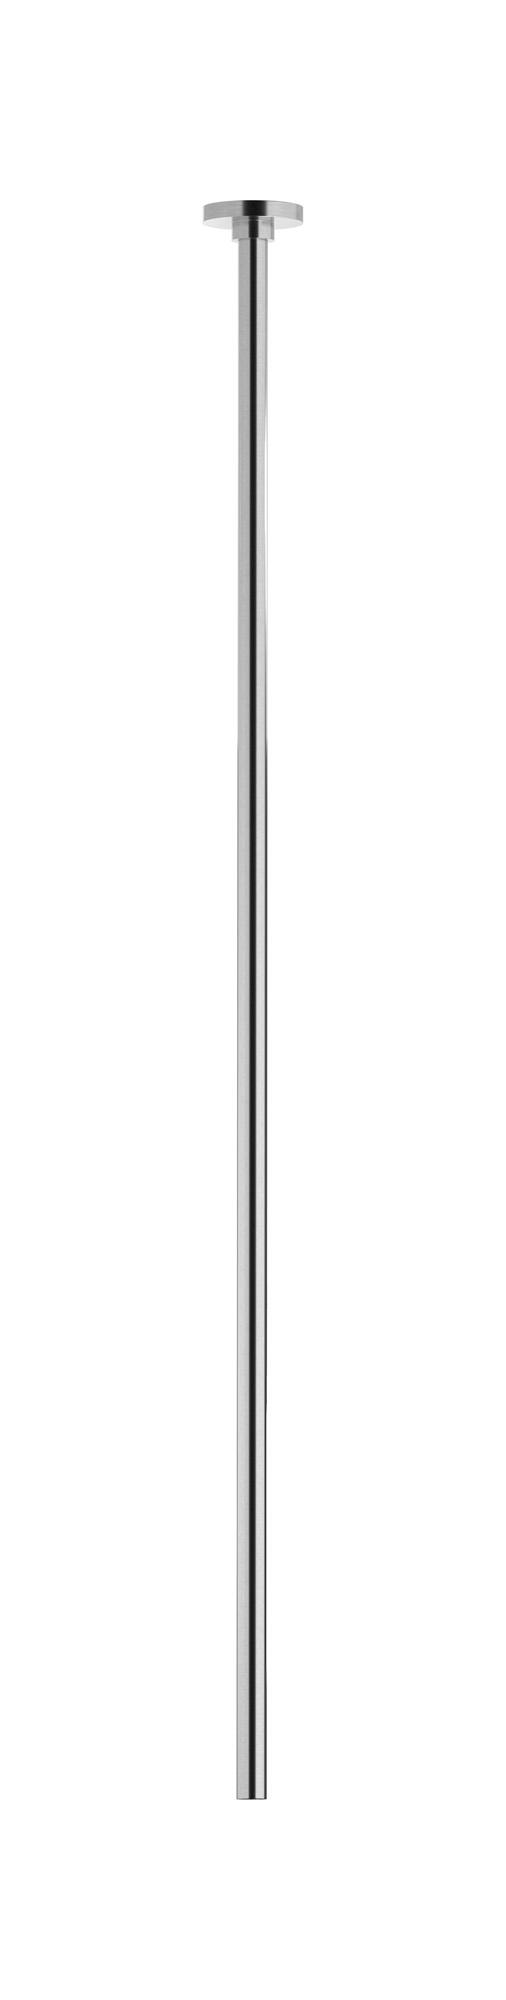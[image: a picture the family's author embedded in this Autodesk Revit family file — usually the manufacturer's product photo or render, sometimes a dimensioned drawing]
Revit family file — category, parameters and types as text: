
# Revit family: RX210
name_source: partatom
category: Apparecchi idraulici
units: mm (PartAtom-declared; Revit-internal decimal feet)

## family parameters
Basato su piano di lavoro = No
Condiviso = No
Mantieni orientamento annotazione = No
Numero OmniClass = 23.45.55.17
Punto di calcolo locali = No
Quota connettore circolare = Usa diametro
Sempre verticale = Sì
Taglio con vuoti quando caricato = No
Tipo di parte = Normale
Titolo OmniClass = Mixing Faucets

## types (12) — shared parameters
Commenti sul tipo = Ceiling spout
Connessione CW = No
Connessione HW = No
Connessione di scarico = No
Connessione di ventilazione = No
Descrizione = Ceiling spout
Produttore = IB Rubinetterie S.p.A.
URL = https://www.weareib.it
Water inlet = 10 mm  [stored 0.0328084 ft]
zero-valued in all types: Prospetto di default

## per-type parameters (varying)
| type | Finishes surface | Immagine tipo | Modello |
| Chrome | IB_Chrome | RX210CC.jpg | RX210CC |
| Black Chrome | IB_Black chrome | RX210CF.jpg | RX210CF |
| Brushed Black Chrome | IB_Brushed black chrome | RX210CS.jpg | RX210CS |
| Pale Gold | IB_Pale gold | RX210II.jpg | RX210II |
| Brushed Pale Gold | IB_brushed pale gold | RX210IS.jpg | RX210IS |
| Matt Black | IB_matt black | RX210NP.jpg | RX210NP |
| Natural Brass | IB_Brass | RX210ON.jpg | RX210ON |
| Gold | IB_gold | RX210OO.jpg | RX210OO |
| Brushed Gold | IB_brushed gold | RX210OS.jpg | RX210OS |
| Rose Gold | IB_Rose gold | RX210RS.jpg | RX210RS |
| Brushed Rose Gold | IB_Brushed rose gold | RX210SR.jpg | RX210SR |
| Brushed Nickel | IB_Brushed nickel | RX210SS.jpg | RX210SS |

note: [stored X ft] marks values corroborated as IEEE doubles in the binary element streams (Revit-internal decimal feet)
